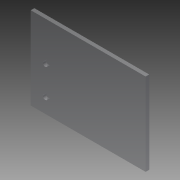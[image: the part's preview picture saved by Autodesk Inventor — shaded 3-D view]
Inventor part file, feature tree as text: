
AUTODESK INVENTOR PART (.ipt)
format: ipt  version: 2014 (Build 180170000, 170)  size: 82,432 bytes
history: native  units: in
note: dims shown in document units (in); Inventor stores cm internally (conversion verified against a paired STEP export)
features: extrude x1, sketch x1
ambient origin geometry x8: Origin, YZ Plane, XZ Plane, XY Plane, X Axis, Y Axis, Z Axis, Center Point
bodies: Solid1 (feature_tree)
feature tree (2):
  extrude  "Extrusion1"  Depth=2.875in
  sketch  "Sketch1"  dims[d2=0.163in d3=0.163in d4=0.5in d5=0.5in d6=1.0in d7=0.125in d8=0.0in d9=1.0in d10=2.0in d11=2.0in d12=2.875in]
